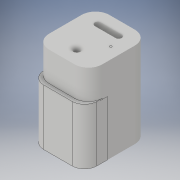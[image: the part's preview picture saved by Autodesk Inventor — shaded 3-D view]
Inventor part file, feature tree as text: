
AUTODESK INVENTOR PART (.ipt)
format: ipt  version: 2017 (Build 210142000, 142)  size: 425,472 bytes
history: native  units: in
note: dims shown in document units (in); Inventor stores cm internally (conversion verified against a paired STEP export)
features: extrude x17, sketch x15, other x3
ambient origin geometry x8: Origin, YZ Plane, XZ Plane, XY Plane, X Axis, Y Axis, Z Axis, Center Point
bodies: body (feature_tree)
feature tree (35):
  extrude  "bace bottom"  Depth=0.2457in
  extrude  "sharpener top"  Depth=0.0828in
  other  "sharpener hole"
  extrude  "Extrusion of sharpener hole"  TaperAngle=90.0deg  [1 undecoded]
  extrude  "pencil holder"  Depth=0.0545in TaperAngle=0.0deg
  extrude  "pencil holder bottom"  Depth=0.0408in TaperAngle=0.0deg
  extrude  "sharpened light hole"  Depth=0.0081in
  extrude  "sharpened light indicator"  Depth=0.0081in
  extrude  "bottom of bace"  Depth=0.0067in
  extrude  "cut for holder"  Depth=0.0042in
  extrude  "bottom of tray slot"  Depth=0.0373in
  sketch  "Sketch15"  dims[d44=0.0641in d45=0.0373in]
  extrude  "nobes for connection"  Depth=0.0155in
  extrude  "connection to nobes"  Depth=0.0108in
  extrude  "holding slot bottom"  Depth=0.0625in
  extrude  "holding slot back"  Depth=0.0625in
  extrude  "holding slot back cut"  Depth=0.0062in
  extrude  "container for wasts"  Depth=0.0625in TaperAngle=0.0deg
  extrude  "holding area top"  Depth=0.008in TaperAngle=0.0deg
  sketch  "Sketch3"  dims[d7=0.288in d8=0.0in d9=0.2457in]
  sketch  "Sketch6"  dims[d11=0.1593in d12=0.0828in]
  sketch  "Sketch7"  dims[d13=0.1819in d14=0.0in d16=90.0deg]
  sketch  "Sketch8"  dims[d17=0.0625in d18=0.0in d19=0.0545in d20=0.0in]
  sketch  "Sketch9"  dims[d22=0.0625in d23=0.0in d25=0.0408in d26=0.0in]
  sketch  "Sketch10"  dims[d29=0.0081in d30=0.0081in]
  sketch  "Sketch12"  dims[d31=0.0081in d32=0.0081in]
  sketch  "Sketch13"  dims[d33=0.0067in d34=0.0509in]
  other  "light indicator"
  sketch  "Sketch14"  dims[d37=0.0794in d39=0.0042in]
  other  "container"
  sketch  "Sketch16"  dims[d47=0.1616in d48=0.0155in]
  sketch  "Sketch18"  dims[d50=0.0769in d51=0.0108in]
  sketch  "Sketch19"  dims[d52=0.0625in d53=0.0in d54=0.0127in]
  sketch  "Sketch20"  dims[d55=0.0625in d56=0.0in d57=0.0133in]
  sketch  "Sketch21"  dims[d59=0.0266in d60=0.0133in d61=0.0625in d62=0.0in d63=0.008in d64=0.0in d66=0.0705in d67=0.0in d68=0.018in d69=0.0052in d70=0.0243in d71=0.0in d74=0.008in d75=0.0in d76=0.0349in d77=0.0314in d78=0.0523in d79=0.0038in d80=0.0064in d81=0.0in d86=0.0062in d87=0.0062in d88=0.0062in d89=0.0062in d90=0.2051in d91=0.0in d92=0.0258in d93=0.0251in d94=0.2051in d95=0.0in d97=0.0062in d98=0.0in]
note: 1 required parameter value undecoded (feature->parameter linkage not recoverable at this tier; creation-order binding heuristic only, values carry confidence <= 0.55)
